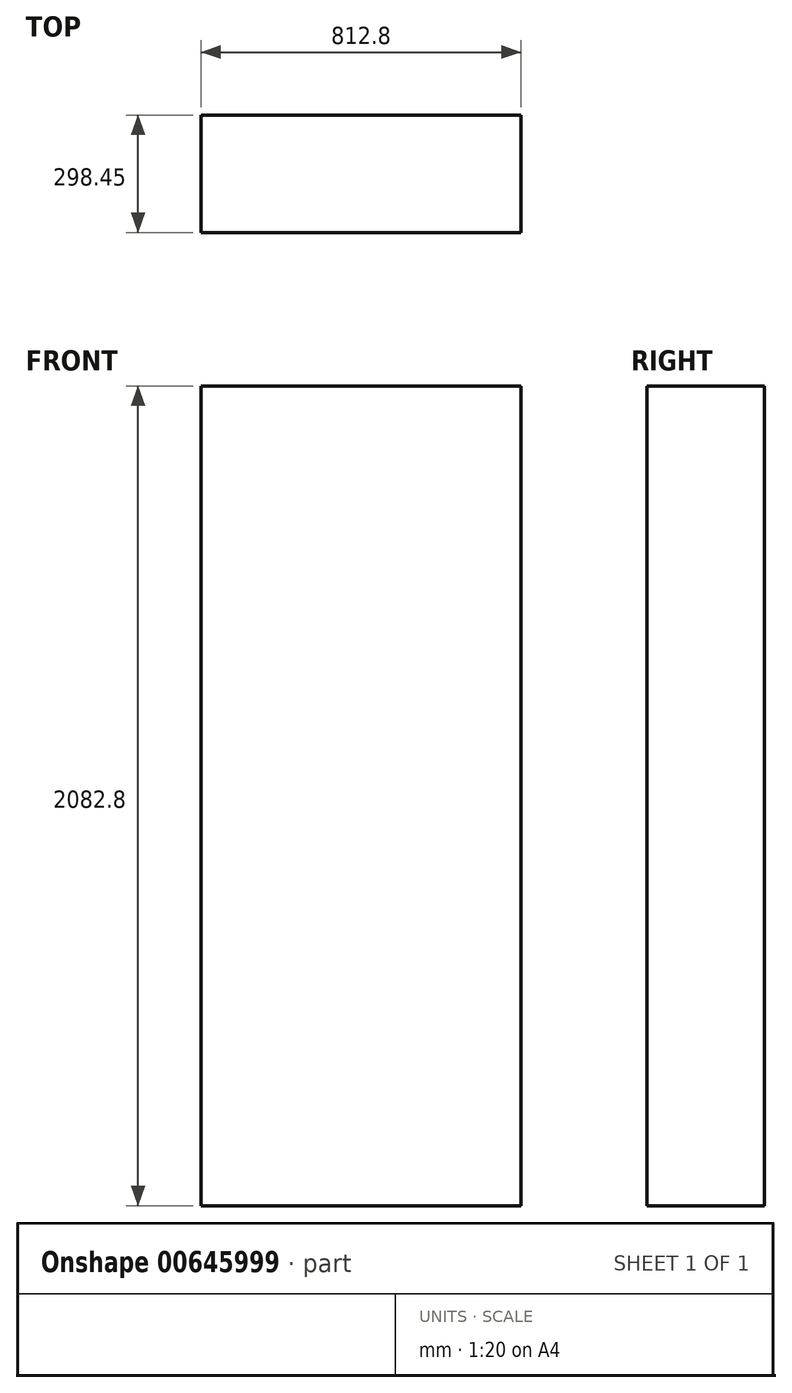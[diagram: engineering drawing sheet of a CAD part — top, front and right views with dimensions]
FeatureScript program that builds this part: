
annotation { "Feature Type Name" : "Feature", "Feature Type Description" : "" }
export const myFeature = defineFeature(function(context is Context, id is Id, definition is map)
    precondition{}
    {
        {
            var Q0;
            Q0=qCreatedBy(makeId("Top.planeOp"),FACE);
            var sketch = newSketch(context, id + "F0", { "sketchPlane" : qUnion([Q0])});
            skLineSegment(sketch, "E0.bottom", {"start": v(0, 0) * mm, "end": v(-812.8, 0) * mm});
            skLineSegment(sketch, "E0.top", {"start": v(0, -298.45) * mm, "end": v(-812.8, -298.45) * mm});
            skLineSegment(sketch, "E0.left", {"start": v(0, 0) * mm, "end": v(0, -298.45) * mm});
            skLineSegment(sketch, "E0.right", {"start": v(-812.8, 0) * mm, "end": v(-812.8, -298.45) * mm});
            skSolve(sketch);
        }
        {
            var Q0;
            Q0=makeQuery(id+"F0.imprint","IMPRINT",FACE,{"disambiguationData":[TD([[makeQuery(id+"F0.imprint","IMPRINT",EDGE,{"derivedFrom":sQuery(id+"F0.wireOp",EDGE,"E0.bottom")}),1.0]])]});
            extrude(context, id + "F1", {"entities" : qUnion([Q0]), "depth" : 2082.8 * mm, "offsetDistance" : 25.4 * mm});
        }
    });
